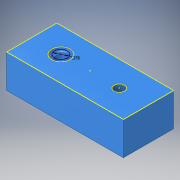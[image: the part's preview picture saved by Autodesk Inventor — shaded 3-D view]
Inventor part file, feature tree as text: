
AUTODESK INVENTOR PART (.ipt)
format: ipt  version: 2018 (Build 220112000, 112)  size: 135,168 bytes
history: native  units: in
note: dims shown in document units (in); Inventor stores cm internally (conversion verified against a paired STEP export)
features: sketch x3, projected_geometry x2, extrude x1, revolve x1
ambient origin geometry x8: Origin, YZ Plane, XZ Plane, XY Plane, X Axis, Y Axis, Z Axis, Center Point
bodies: Body1 (feature_tree)
feature tree (7):
  extrude  "Extrusion5"  Depth=3.5in
  revolve  "Revolution1"  [1 undecoded]
  sketch  "Sketch9"  dims[d22=0.875in d23=0.875in d24=1.0in d25=0.0in d34=0.139in d35=0.05in d36=90.0deg d37=0.378in]
  sketch  "Sketch1"  dims[d3=1.5in d4=3.5in]
  sketch  "Sketch8"  dims[d20=0.3125in d21=1.0in]
  projected_geometry  "Projected Loop5"
  projected_geometry  "Projected Loop6"
note: 1 required parameter value undecoded (feature->parameter linkage not recoverable at this tier; creation-order binding heuristic only, values carry confidence <= 0.55)
